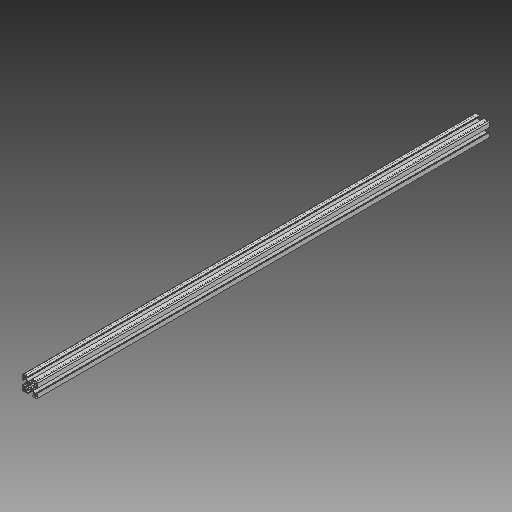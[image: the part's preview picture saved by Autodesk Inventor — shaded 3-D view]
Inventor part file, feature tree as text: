
AUTODESK INVENTOR PART (.ipt)
format: ipt  version: 2018 (Build 220112000, 112)  size: 288,256 bytes
history: native  units: mm
features: sketch x2, other x2, extrude x1, reference x1
ambient origin geometry x8: Origin, YZ Plane, XZ Plane, XY Plane, X Axis, Y Axis, Z Axis, Center Point
bodies: Solid1 (feature_tree)
feature tree (6):
  extrude  "Extrusion1"  [1 undecoded]
  sketch  "Sketch2"
  sketch  "Sketch1"  dims[d0=900.0mm d1=0.0mm]
  reference  "Reference1"
  other  "<userpath>\OneDrive\Inventor\Beast 3D Printer\Assembly3.iam"
  other  "Assembly3.iam"
note: 1 required parameter value undecoded (feature->parameter linkage not recoverable at this tier; creation-order binding heuristic only, values carry confidence <= 0.55)
